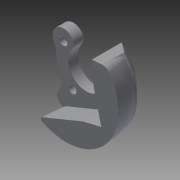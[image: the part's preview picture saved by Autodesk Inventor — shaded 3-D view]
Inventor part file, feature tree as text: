
AUTODESK INVENTOR PART (.ipt)
format: ipt  version: 2015 SP1 (Build 190203100, 203)  size: 325,120 bytes
history: native  units: in
note: dims shown in document units (in); Inventor stores cm internally (conversion verified against a paired STEP export)
features: fillet x5, sketch x4, extrude x3, chamfer x3, other x2, hole x2, mirror x1, projected_geometry x1
ambient origin geometry x8: Origin, YZ Plane, XZ Plane, XY Plane, X Axis, Y Axis, Z Axis, Center Point
bodies: Solid1 (feature_tree)
feature tree (21):
  other  "mount_alt.ipt"
  other  "mount_sketch_alt.ipt"
  extrude  "Extrusion1"  Depth=0.3937in
  extrude  "Extrusion2"  Depth=2.2425in
  hole  "Hole1"  [1 undecoded]
  hole  "Hole2"  [1 undecoded]
  chamfer  "Chamfer1"  Distance=0.9055in
  fillet  "Fillet1"  Radius=0.25in
  chamfer  "Chamfer2"  Distance=2.6251in
  chamfer  "Chamfer3"  Distance=0.5in
  fillet  "Fillet2"  Radius=0.2in
  fillet  "Fillet3"  Radius=0.2in
  fillet  "Fillet4"  Radius=0.2in
  mirror  "Mirror1"
  extrude  "Extrusion3"  Depth=0.5in TaperAngle=45.0deg
  fillet  "Fillet5"  Radius=1.125in
  sketch  "Sketch19"  dims[d70=0.0312in d78=0.8352in d79=0.8352in d80=0.8352in d81=0.8352in d82=0.8352in d83=0.8352in d84=0.0232in d85=0.0075in d87=30.0deg d88=0.5in d89=0.6693in d3=2.4676in d4=0.9055in d6=0.25in d7=0.0in d8=2.6251in d9=0.5in d10=0.0in d33=1.0in d34=1.0in d13=0.201in d14=0.75in d15=0.385in d16=0.125in d17=0.5635in d18=1.0in d19=0.8108in d37=1.0in d38=1.0in d22=0.201in d23=0.75in d24=0.385in d25=0.125in d26=0.5635in d27=1.0in d28=0.8108in d29=0.2in d30=0.125in d31=45.0deg d32=0.2in d35=0.2in d36=0.125in d39=45.0deg d40=0.5in d41=0.05in d42=45.0deg d43=1.125in d44=0.2in d45=0.05in d46=0.0855in d47=0.5in d48=0.0in d49=0.2in]
  sketch  "Sketch2"  dims[d0=0.3937in d1=0.3937in]
  sketch  "Sketch3"  dims[d2=3.5433in d57=2.2425in d58=1.75in]
  sketch  "Sketch4"  dims[d67=0.7543in]
  projected_geometry  "Projected Loop2"
note: 2 required parameter values undecoded (feature->parameter linkage not recoverable at this tier; creation-order binding heuristic only, values carry confidence <= 0.55)
